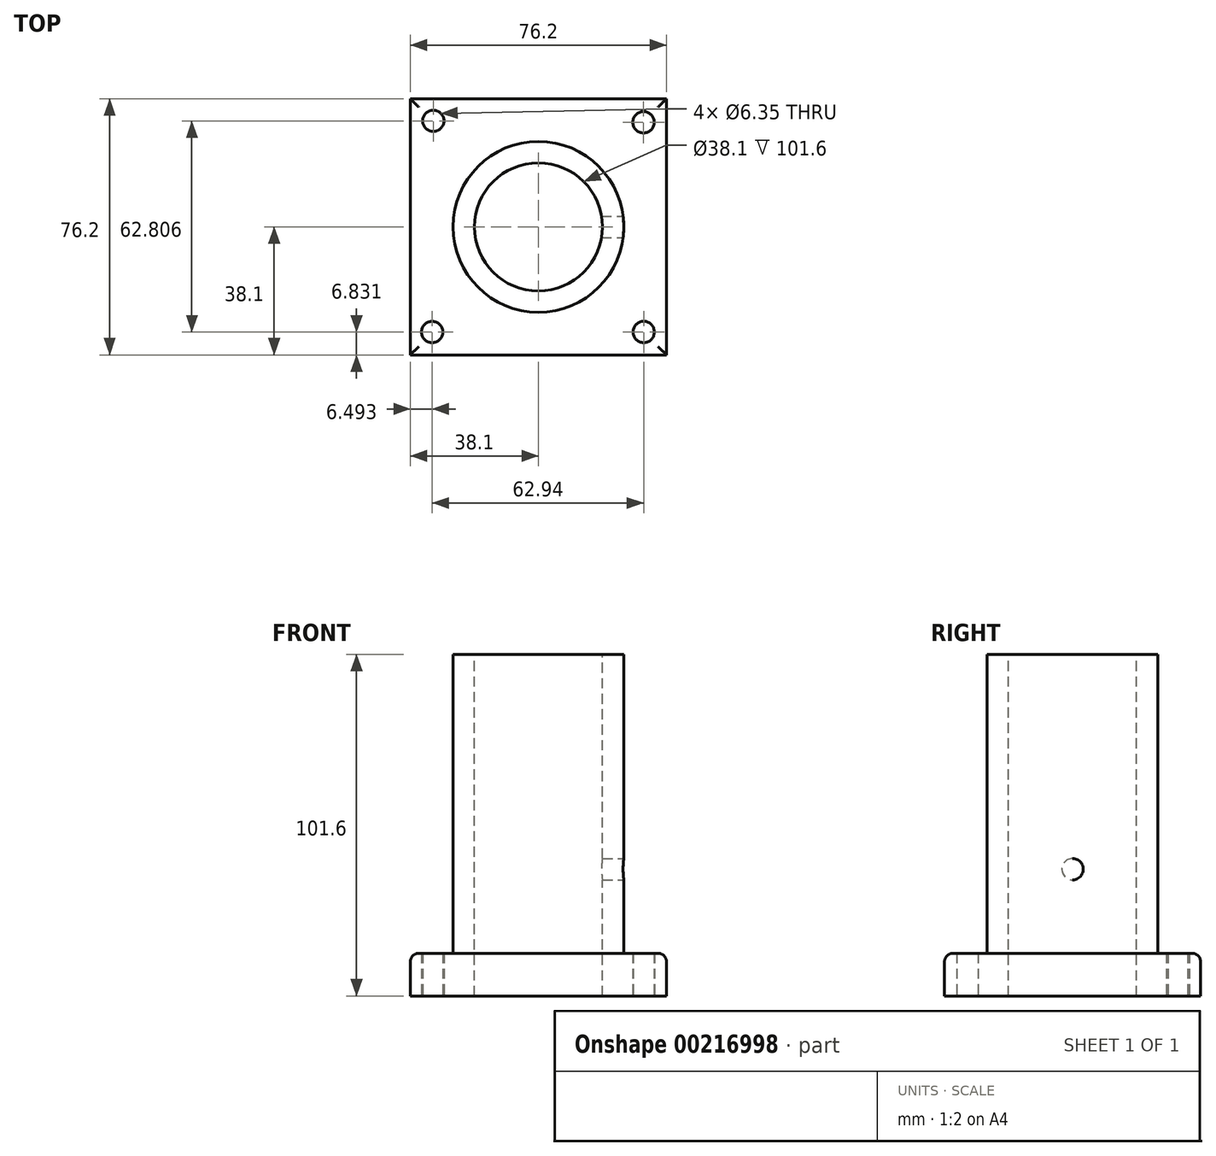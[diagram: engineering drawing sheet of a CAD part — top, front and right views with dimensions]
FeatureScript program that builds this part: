
annotation { "Feature Type Name" : "Feature", "Feature Type Description" : "" }
export const myFeature = defineFeature(function(context is Context, id is Id, definition is map)
    precondition{}
    {
        {
            var Q0;
            Q0=qCreatedBy(makeId("Top.planeOp"),FACE);
            var sketch = newSketch(context, id + "F0", { "sketchPlane" : qUnion([Q0])});
            skLineSegment(sketch, "E0.bottom", {"start": v(38.1, -38.1) * mm, "end": v(-38.1, -38.1) * mm});
            skLineSegment(sketch, "E0.top", {"start": v(38.1, 38.1) * mm, "end": v(-38.1, 38.1) * mm});
            skLineSegment(sketch, "E0.left", {"start": v(38.1, -38.1) * mm, "end": v(38.1, 38.1) * mm});
            skLineSegment(sketch, "E0.right", {"start": v(-38.1, -38.1) * mm, "end": v(-38.1, 38.1) * mm});
            skPoint(sketch, "E0.middle", {"position": v(0, 0) * mm});
            skLineSegment(sketch, "E1.bottom", {"start": v(25.4, -25.4) * mm, "end": v(-25.4, -25.4) * mm});
            skLineSegment(sketch, "E1.top", {"start": v(25.4, 25.4) * mm, "end": v(-25.4, 25.4) * mm});
            skLineSegment(sketch, "E1.left", {"start": v(25.4, -25.4) * mm, "end": v(25.4, 25.4) * mm});
            skLineSegment(sketch, "E1.right", {"start": v(-25.4, -25.4) * mm, "end": v(-25.4, 25.4) * mm});
            skCircle(sketch, "E2", {"center": v(-31.27, 31.54) * mm, "radius": 3.18 * mm});
            skCircle(sketch, "E3", {"center": v(31.28, 31.1) * mm, "radius": 3.18 * mm});
            skCircle(sketch, "E4", {"center": v(-31.6, -31.27) * mm, "radius": 3.18 * mm});
            skCircle(sketch, "E5", {"center": v(31.33, -31.26) * mm, "radius": 3.18 * mm});
            skCircle(sketch, "E6", {"center": v(62.75, -55.76) * mm, "radius": 3.18 * mm});
            skSolve(sketch);
        }
        {
            var Q0;
            Q0=makeQuery(id+"F0.imprint","IMPRINT",FACE,{"disambiguationData":[TD([[makeQuery(id+"F0.imprint","IMPRINT",EDGE,{"derivedFrom":sQuery(id+"F0.wireOp",EDGE,"E1.bottom")}),-1.0]])]});
            extrude(context, id + "F1", {"entities" : qUnion([Q0]), "depth" : 101.6 * mm});
        }
        {
            var Q0;
            Q0=makeQuery(id+"F0.imprint","IMPRINT",FACE,{"disambiguationData":[TD([[makeQuery(id+"F0.imprint","IMPRINT",EDGE,{"derivedFrom":sQuery(id+"F0.wireOp",EDGE,"E0.bottom")}),-1.0]])]});
            extrude(context, id + "F2", {"entities" : qUnion([Q0]), "operationType" : NewBodyOperationType.ADD, "depth" : 12.7 * mm});
        }
        {
            var Q0;
            Q0=makeQuery(id+"F1.opExtrude","CAP_FACE",FACE,{"disambiguationData":[OSD([sQuery(id+"F0.wireOp",EDGE,"E1.bottom"),sQuery(id+"F0.wireOp",EDGE,"E1.top"),sQuery(id+"F0.wireOp",EDGE,"E1.left"),sQuery(id+"F0.wireOp",EDGE,"E1.right")])],"isStart":false});
            var sketch = newSketch(context, id + "F3", { "sketchPlane" : qUnion([Q0])});
            skCircle(sketch, "E7", {"center": v(0, 0) * mm, "radius": 19.05 * mm});
            skSolve(sketch);
        }
        {
            var Q0;
            Q0=makeQuery(id+"F3.imprint","IMPRINT",FACE,{"disambiguationData":[TD([[makeQuery(id+"F3.imprint","IMPRINT",EDGE,{"derivedFrom":sQuery(id+"F3.wireOp",EDGE,"E7")}),1.0]])]});
            extrude(context, id + "F4", {"entities" : qUnion([Q0]), "operationType" : NewBodyOperationType.REMOVE, "endBound" : BoundingType.THROUGH_ALL, "oppositeDirection" : true, "depth" : 25.4 * mm});
        }
        {
            var Q0;
            Q0=makeQuery(id+"F1.opExtrude","SWEPT_FACE",FACE,{"disambiguationData":[OSD([sQuery(id+"F0.wireOp",EDGE,"E1.left")])]});
            var sketch = newSketch(context, id + "F5", { "sketchPlane" : qUnion([Q0])});
            skCircle(sketch, "E8", {"center": v(0, 37.7) * mm, "radius": 3.18 * mm});
            skSolve(sketch);
        }
        {
            var Q0;
            Q0=makeQuery(id+"F5.imprint","IMPRINT",FACE,{"disambiguationData":[TD([[makeQuery(id+"F5.imprint","IMPRINT",EDGE,{"derivedFrom":sQuery(id+"F5.wireOp",EDGE,"E8")}),1.0]])]});
            extrude(context, id + "F6", {"entities" : qUnion([Q0]), "operationType" : NewBodyOperationType.REMOVE, "oppositeDirection" : true, "depth" : 25.4 * mm});
        }
        {
            var Q0;
            Q0=makeQuery(id+"F1.opExtrude","SWEPT_EDGE",EDGE,{"disambiguationData":[OSD([sQuery(id+"F0.wireOp",EDGE,"E1.bottom"),sQuery(id+"F0.wireOp",EDGE,"E1.left")])]});
            var Q1;
            Q1=makeQuery(id+"F1.opExtrude","SWEPT_EDGE",EDGE,{"disambiguationData":[OSD([sQuery(id+"F0.wireOp",EDGE,"E1.top"),sQuery(id+"F0.wireOp",EDGE,"E1.left")])]});
            var Q2;
            Q2=makeQuery(id+"F1.opExtrude","SWEPT_EDGE",EDGE,{"disambiguationData":[OSD([sQuery(id+"F0.wireOp",EDGE,"E1.bottom"),sQuery(id+"F0.wireOp",EDGE,"E1.right")])]});
            var Q3;
            Q3=makeQuery(id+"F1.opExtrude","SWEPT_EDGE",EDGE,{"disambiguationData":[OSD([sQuery(id+"F0.wireOp",EDGE,"E1.top"),sQuery(id+"F0.wireOp",EDGE,"E1.right")])]});
            fillet(context, id + "F7", {"entities" : qUnion([Q0, Q1, Q2, Q3]), "radius" : 25.4 * mm, "tangentPropagation" : true, "allowEdgeOverflow" : false});
        }
        {
            var Q0;
            Q0=makeQuery(id+"F2.opExtrude","CAP_EDGE",EDGE,{"disambiguationData":[OSD([sQuery(id+"F0.wireOp",EDGE,"E0.bottom")])],"isStart":false});
            var Q1;
            Q1=makeQuery(id+"F2.opExtrude","CAP_EDGE",EDGE,{"disambiguationData":[OSD([sQuery(id+"F0.wireOp",EDGE,"E0.left")])],"isStart":false});
            var Q2;
            Q2=makeQuery(id+"F2.opExtrude","CAP_EDGE",EDGE,{"disambiguationData":[OSD([sQuery(id+"F0.wireOp",EDGE,"E0.right")])],"isStart":false});
            var Q3;
            Q3=makeQuery(id+"F2.opExtrude","CAP_EDGE",EDGE,{"disambiguationData":[OSD([sQuery(id+"F0.wireOp",EDGE,"E0.top")])],"isStart":false});
            fillet(context, id + "F8", {"entities" : qUnion([Q0, Q1, Q2, Q3]), "radius" : 2.54 * mm, "tangentPropagation" : true, "allowEdgeOverflow" : false});
        }
    });
